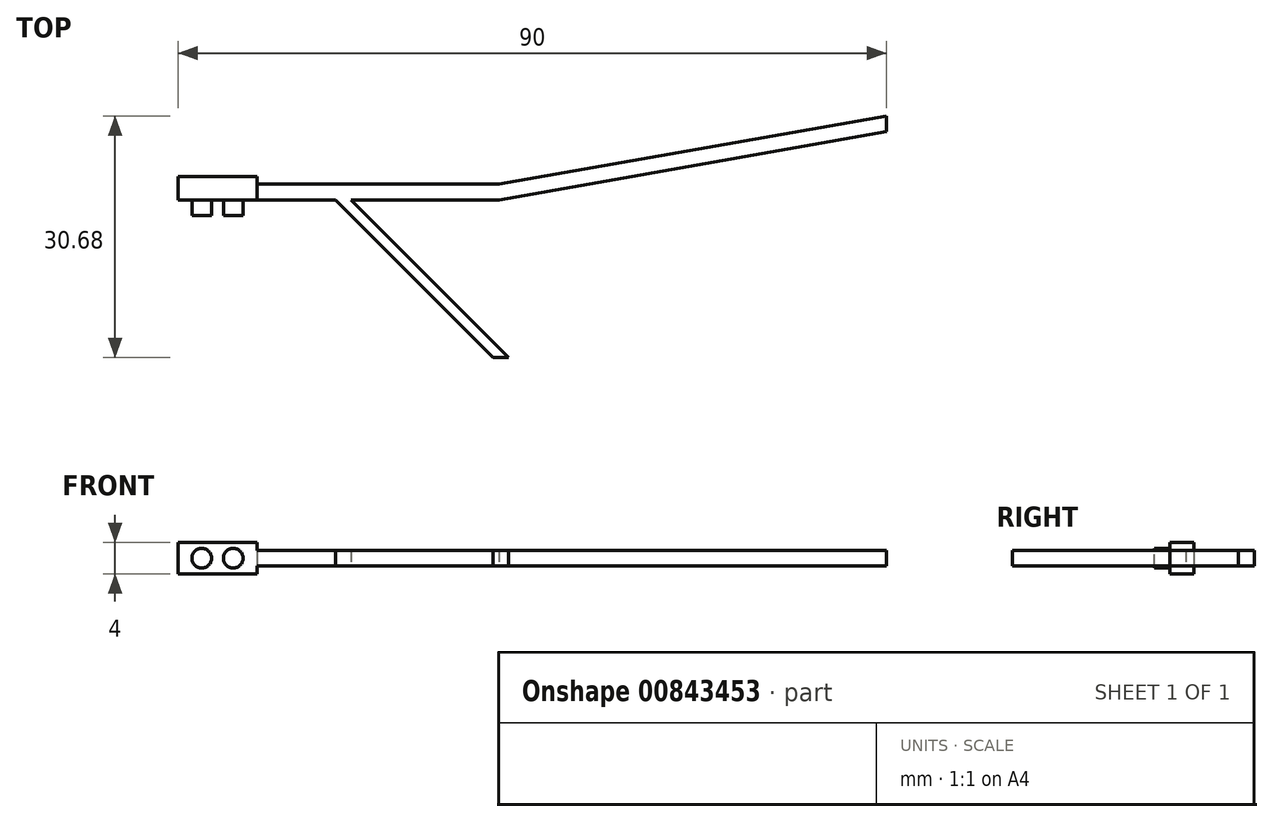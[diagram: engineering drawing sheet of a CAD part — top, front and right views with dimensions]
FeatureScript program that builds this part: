
annotation { "Feature Type Name" : "Feature", "Feature Type Description" : "" }
export const myFeature = defineFeature(function(context is Context, id is Id, definition is map)
    precondition{}
    {
        {
            var Q0;
            Q0=qCreatedBy(makeId("Top.planeOp"),FACE);
            var sketch = newSketch(context, id + "F0", { "sketchPlane" : qUnion([Q0])});
            skLineSegment(sketch, "E0.bottom", {"start": v(0, 0) * mm, "end": v(10, 0) * mm});
            skLineSegment(sketch, "E0.top", {"start": v(0, 3) * mm, "end": v(10, 3) * mm});
            skLineSegment(sketch, "E0.left", {"start": v(0, 0) * mm, "end": v(0, 3) * mm});
            skLineSegment(sketch, "E0.right", {"start": v(10, 0) * mm, "end": v(10, 3) * mm});
            skPoint(sketch, "E1", {"position": v(10, 2) * mm});
            skLineSegment(sketch, "E2", {"start": v(10, 2) * mm, "end": v(10, 0) * mm});
            skLineSegment(sketch, "E3.bottom", {"start": v(10, 2) * mm, "end": v(40.76, 2) * mm});
            skLineSegment(sketch, "E3.top", {"start": v(10, 0) * mm, "end": v(40.76, 0) * mm});
            skLineSegment(sketch, "E3.right", {"start": v(40.76, 2) * mm, "end": v(40.76, 0) * mm});
            skLineSegment(sketch, "E4", {"start": v(40.76, 0) * mm, "end": v(90, 8.68) * mm});
            skLineSegment(sketch, "E5", {"start": v(40.76, 2) * mm, "end": v(90, 10.68) * mm});
            skLineSegment(sketch, "E6", {"start": v(90, 10.68) * mm, "end": v(90, 8.68) * mm});
            skLineSegment(sketch, "E7", {"start": v(90, 0) * mm, "end": v(90, 10.68) * mm});
            skSolve(sketch);
        }
        {
            var Q0;
            Q0=makeQuery(id+"F0.imprint","IMPRINT",FACE,{"disambiguationData":[TD([[makeQuery(id+"F0.imprint","IMPRINT",EDGE,{"derivedFrom":sQuery(id+"F0.wireOp",EDGE,"E3.right")}),1.0]])]});
            var Q1;
            Q1=makeQuery(id+"F0.imprint","IMPRINT",FACE,{"disambiguationData":[TD([[makeQuery(id+"F0.imprint","IMPRINT",EDGE,{"derivedFrom":sQuery(id+"F0.wireOp",EDGE,"zCZAbvF0-64Di-gtxW-A2sx-DfSDvnBLB7fd.bottom")}),1.0]])]});
            var Q2;
            Q2=makeQuery(id+"F0.imprint","IMPRINT",FACE,{"disambiguationData":[TD([[makeQuery(id+"F0.imprint","IMPRINT",EDGE,{"derivedFrom":sQuery(id+"F0.wireOp",EDGE,"E3.bottom")}),-1.0]])]});
            extrude(context, id + "F1", {"entities" : qUnion([Q0, Q1, Q2]), "depth" : 2 * mm, "offsetDistance" : 25 * mm});
        }
        {
            var Q0;
            Q0=makeQuery(id+"F0.imprint","IMPRINT",FACE,{"disambiguationData":[TD([[makeQuery(id+"F0.imprint","IMPRINT",EDGE,{"derivedFrom":sQuery(id+"F0.wireOp",EDGE,"E0.bottom")}),1.0]])]});
            extrude(context, id + "F2", {"entities" : qUnion([Q0]), "operationType" : NewBodyOperationType.ADD, "depth" : 3 * mm, "offsetDistance" : 25 * mm, "hasSecondDirection" : true, "secondDirectionOppositeDirection" : true, "secondDirectionDepth" : 1 * mm});
        }
        {
            var Q0;
            Q0=makeQuery(id+"F1.opExtrude","SWEPT_FACE",FACE,{"disambiguationData":[OSD([sQuery(id+"F0.wireOp",EDGE,"E0.bottom"),sQuery(id+"F0.wireOp",EDGE,"E3.top")])]});
            var sketch = newSketch(context, id + "F3", { "sketchPlane" : qUnion([Q0])});
            skPoint(sketch, "E8", {"position": v(10, 0) * mm});
            skLineSegment(sketch, "E9", {"start": v(10, 0) * mm, "end": v(10, 2) * mm});
            skPoint(sketch, "E10", {"position": v(10, 1) * mm});
            skLineSegment(sketch, "E11", {"start": v(10, 1) * mm, "end": v(0, 1) * mm});
            skPoint(sketch, "E12", {"position": v(5, 1) * mm});
            skPoint(sketch, "E13", {"position": v(3, 1) * mm});
            skLineSegment(sketch, "E14", {"start": v(5, 1) * mm, "end": v(5, 3) * mm});
            skLineSegment(sketch, "E15.MirrorCS", {"start": v(5, 1) * mm, "end": v(5, -1) * mm});
            skCircle(sketch, "E16", {"center": v(3, 1) * mm, "radius": 1.25 * mm});
            skPoint(sketch, "E17.MirrorP", {"position": v(7, 1) * mm});
            skCircle(sketch, "E18.MirrorC", {"center": v(7, 1) * mm, "radius": 1.25 * mm});
            skSolve(sketch);
        }
        {
            var Q0;
            Q0 = qSketchRegion(id + "F3", true);
            extrude(context, id + "F4", {"entities" : qUnion([Q0]), "operationType" : NewBodyOperationType.ADD, "depth" : 2 * mm, "offsetDistance" : 25 * mm});
        }
        {
            var Q0;
            Q0=qCreatedBy(makeId("Top.planeOp"),FACE);
            var sketch = newSketch(context, id + "F5", { "sketchPlane" : qUnion([Q0])});
            skPoint(sketch, "E19", {"position": v(22, 0) * mm});
            skLineSegment(sketch, "E20", {"start": v(22, 0) * mm, "end": v(42, -20) * mm});
            skLineSegment(sketch, "E21", {"start": v(42, -20) * mm, "end": v(42, 0) * mm});
            skPoint(sketch, "E22", {"position": v(0, 0) * mm});
            skPoint(sketch, "E23", {"position": v(10, 0) * mm});
            skLineSegment(sketch, "E24", {"start": v(0, 0) * mm, "end": v(10, 0) * mm});
            skPoint(sketch, "E25", {"position": v(5, 0) * mm});
            skPoint(sketch, "E26", {"position": v(20, 0) * mm});
            skLineSegment(sketch, "E27", {"start": v(20, 0) * mm, "end": v(40, -20) * mm});
            skLineSegment(sketch, "E28", {"start": v(40, -20) * mm, "end": v(42, -20) * mm});
            skLineSegment(sketch, "E29", {"start": v(20, 0) * mm, "end": v(22, 0) * mm});
            skSolve(sketch);
        }
        {
            var Q0;
            Q0 = qSketchRegion(id + "F5", true);
            extrude(context, id + "F6", {"entities" : qUnion([Q0]), "operationType" : NewBodyOperationType.ADD, "depth" : 2 * mm, "offsetDistance" : 25 * mm});
        }
    });
